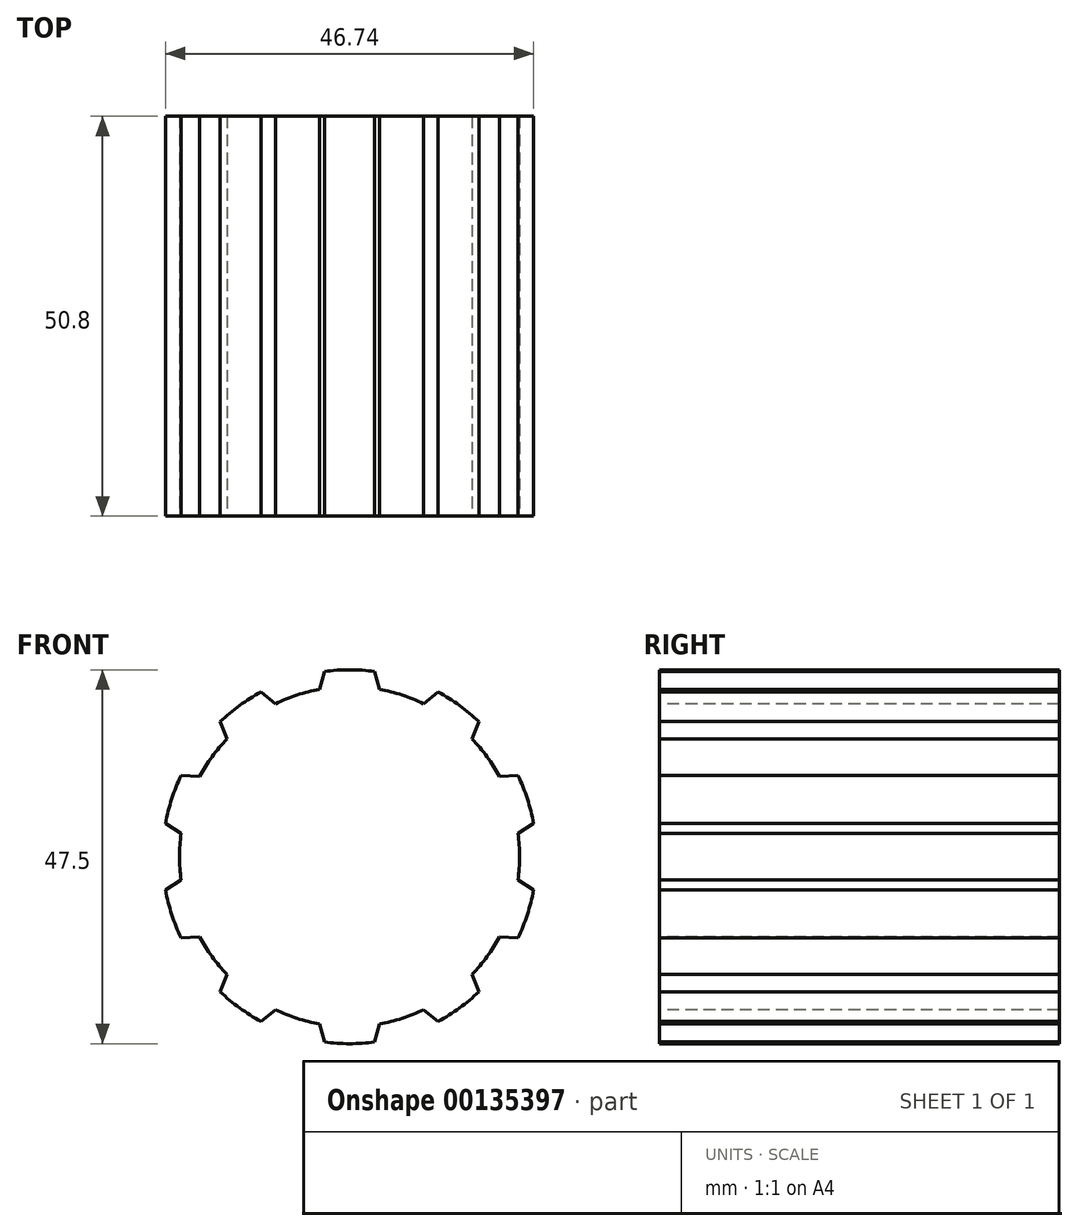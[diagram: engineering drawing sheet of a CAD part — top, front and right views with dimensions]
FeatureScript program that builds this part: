
annotation { "Feature Type Name" : "Feature", "Feature Type Description" : "" }
export const myFeature = defineFeature(function(context is Context, id is Id, definition is map)
    precondition{}
    {
        {
            var Q0;
            Q0=qCreatedBy(makeId("Front.planeOp"),FACE);
            var sketch = newSketch(context, id + "F0", { "sketchPlane" : qUnion([Q0])});
            skCircle(sketch, "E0", {"center": v(0, 0) * mm, "radius": 21.59 * mm});
            skArc(sketch, "E1", {"start": v(3.2, 23.53) * mm, "mid": v(0, 23.75) * mm, "end": v(-3.2, 23.53) * mm});
            skLineSegment(sketch, "E2", {"start": v(0, 0) * mm, "end": v(0, 31.16) * mm, "construction": true});
            skLineSegment(sketch, "E3", {"start": v(-3.81, 21.25) * mm, "end": v(-3.2, 23.53) * mm});
            skLineSegment(sketch, "E4.MirrorCS", {"start": v(3.81, 21.25) * mm, "end": v(3.2, 23.53) * mm});
            skLineSegment(sketch, "E5.1.0", {"start": v(-9.4, 19.43) * mm, "end": v(-11.24, 20.92) * mm});
            skArc(sketch, "E5.1.1", {"start": v(-11.24, 20.92) * mm, "mid": v(-13.96, 19.21) * mm, "end": v(-16.42, 17.16) * mm});
            skLineSegment(sketch, "E5.1.2", {"start": v(-15.57, 14.95) * mm, "end": v(-16.42, 17.16) * mm});
            skLineSegment(sketch, "E5.2.0", {"start": v(-19.03, 10.2) * mm, "end": v(-21.4, 10.31) * mm});
            skArc(sketch, "E5.2.1", {"start": v(-21.4, 10.31) * mm, "mid": v(-22.59, 7.34) * mm, "end": v(-23.37, 4.23) * mm});
            skLineSegment(sketch, "E5.2.2", {"start": v(-21.39, 2.94) * mm, "end": v(-23.37, 4.23) * mm});
            skLineSegment(sketch, "E6.1.3.0", {"start": v(-21.39, -2.94) * mm, "end": v(-23.37, -4.23) * mm});
            skArc(sketch, "E6.3.3.0", {"start": v(-23.37, -4.23) * mm, "mid": v(-22.59, -7.34) * mm, "end": v(-21.4, -10.31) * mm});
            skLineSegment(sketch, "E6.7.3.0", {"start": v(-19.03, -10.2) * mm, "end": v(-21.4, -10.31) * mm});
            skLineSegment(sketch, "E6.1.4.0", {"start": v(-15.57, -14.95) * mm, "end": v(-16.42, -17.16) * mm});
            skArc(sketch, "E6.3.4.0", {"start": v(-16.42, -17.16) * mm, "mid": v(-13.96, -19.21) * mm, "end": v(-11.24, -20.92) * mm});
            skLineSegment(sketch, "E6.7.4.0", {"start": v(-9.4, -19.43) * mm, "end": v(-11.24, -20.92) * mm});
            skLineSegment(sketch, "E6.1.5.0", {"start": v(-3.81, -21.25) * mm, "end": v(-3.2, -23.53) * mm});
            skArc(sketch, "E6.3.5.0", {"start": v(-3.2, -23.53) * mm, "mid": v(0, -23.75) * mm, "end": v(3.2, -23.53) * mm});
            skLineSegment(sketch, "E6.7.5.0", {"start": v(3.81, -21.25) * mm, "end": v(3.2, -23.53) * mm});
            skLineSegment(sketch, "E6.1.6.0", {"start": v(9.4, -19.43) * mm, "end": v(11.24, -20.92) * mm});
            skArc(sketch, "E6.3.6.0", {"start": v(11.24, -20.92) * mm, "mid": v(13.96, -19.21) * mm, "end": v(16.42, -17.16) * mm});
            skLineSegment(sketch, "E6.7.6.0", {"start": v(15.57, -14.95) * mm, "end": v(16.42, -17.16) * mm});
            skLineSegment(sketch, "E6.1.7.0", {"start": v(19.03, -10.2) * mm, "end": v(21.4, -10.31) * mm});
            skArc(sketch, "E6.3.7.0", {"start": v(21.4, -10.31) * mm, "mid": v(22.59, -7.34) * mm, "end": v(23.37, -4.23) * mm});
            skLineSegment(sketch, "E6.7.7.0", {"start": v(21.39, -2.94) * mm, "end": v(23.37, -4.23) * mm});
            skLineSegment(sketch, "E6.1.8.0", {"start": v(21.39, 2.94) * mm, "end": v(23.37, 4.23) * mm});
            skArc(sketch, "E6.3.8.0", {"start": v(23.37, 4.23) * mm, "mid": v(22.59, 7.34) * mm, "end": v(21.4, 10.31) * mm});
            skLineSegment(sketch, "E6.7.8.0", {"start": v(19.03, 10.2) * mm, "end": v(21.4, 10.31) * mm});
            skLineSegment(sketch, "E6.1.9.0", {"start": v(15.57, 14.95) * mm, "end": v(16.42, 17.16) * mm});
            skArc(sketch, "E6.3.9.0", {"start": v(16.42, 17.16) * mm, "mid": v(13.96, 19.21) * mm, "end": v(11.24, 20.92) * mm});
            skLineSegment(sketch, "E6.7.9.0", {"start": v(9.4, 19.43) * mm, "end": v(11.24, 20.92) * mm});
            skSolve(sketch);
        }
        {
            var Q0;
            {var subQ0=sQuery(id+"F0.wireOp",EDGE,"E0");var subQ3=makeQuery(id+"F0.imprint","INTERSECT",VERTEX,{"derivedFrom":[subQ0,sQuery(id+"F0.wireOp",EDGE,"E6.1.8.0")]});Q0=makeQuery(id+"F0.imprint","IMPRINT",FACE,{"disambiguationData":[TD([[makeQuery(id+"F0.imprint","IMPRINT",EDGE,{"disambiguationData":[TD([[subQ3,-1.0]])],"derivedFrom":subQ0}),1.0]])]});}
            var Q1;
            Q1=makeQuery(id+"F0.imprint","IMPRINT",FACE,{"disambiguationData":[TD([[makeQuery(id+"F0.imprint","IMPRINT",EDGE,{"derivedFrom":sQuery(id+"F0.wireOp",EDGE,"E1")}),1.0]])]});
            var Q2;
            {var subQ0=sQuery(id+"F0.wireOp",EDGE,"E6.1.9.0");Q2=makeQuery(id+"F0.imprint","IMPRINT",FACE,{"disambiguationData":[TD([[makeQuery(id+"F0.imprint","IMPRINT",EDGE,{"derivedFrom":subQ0}),1.0]])]});}
            var Q3;
            {var subQ0=sQuery(id+"F0.wireOp",EDGE,"E6.1.8.0");Q3=makeQuery(id+"F0.imprint","IMPRINT",FACE,{"disambiguationData":[TD([[makeQuery(id+"F0.imprint","IMPRINT",EDGE,{"derivedFrom":subQ0}),1.0]])]});}
            var Q4;
            {var subQ0=sQuery(id+"F0.wireOp",EDGE,"E6.1.7.0");Q4=makeQuery(id+"F0.imprint","IMPRINT",FACE,{"disambiguationData":[TD([[makeQuery(id+"F0.imprint","IMPRINT",EDGE,{"derivedFrom":subQ0}),1.0]])]});}
            var Q5;
            {var subQ0=sQuery(id+"F0.wireOp",EDGE,"E6.1.6.0");Q5=makeQuery(id+"F0.imprint","IMPRINT",FACE,{"disambiguationData":[TD([[makeQuery(id+"F0.imprint","IMPRINT",EDGE,{"derivedFrom":subQ0}),1.0]])]});}
            var Q6;
            {var subQ0=sQuery(id+"F0.wireOp",EDGE,"E6.1.5.0");Q6=makeQuery(id+"F0.imprint","IMPRINT",FACE,{"disambiguationData":[TD([[makeQuery(id+"F0.imprint","IMPRINT",EDGE,{"derivedFrom":subQ0}),1.0]])]});}
            var Q7;
            {var subQ0=sQuery(id+"F0.wireOp",EDGE,"E6.1.4.0");Q7=makeQuery(id+"F0.imprint","IMPRINT",FACE,{"disambiguationData":[TD([[makeQuery(id+"F0.imprint","IMPRINT",EDGE,{"derivedFrom":subQ0}),1.0]])]});}
            var Q8;
            {var subQ0=sQuery(id+"F0.wireOp",EDGE,"E6.1.3.0");Q8=makeQuery(id+"F0.imprint","IMPRINT",FACE,{"disambiguationData":[TD([[makeQuery(id+"F0.imprint","IMPRINT",EDGE,{"derivedFrom":subQ0}),1.0]])]});}
            var Q9;
            {var subQ0=sQuery(id+"F0.wireOp",EDGE,"E5.2.0");Q9=makeQuery(id+"F0.imprint","IMPRINT",FACE,{"disambiguationData":[TD([[makeQuery(id+"F0.imprint","IMPRINT",EDGE,{"derivedFrom":subQ0}),1.0]])]});}
            var Q10;
            {var subQ0=sQuery(id+"F0.wireOp",EDGE,"E5.1.0");Q10=makeQuery(id+"F0.imprint","IMPRINT",FACE,{"disambiguationData":[TD([[makeQuery(id+"F0.imprint","IMPRINT",EDGE,{"derivedFrom":subQ0}),1.0]])]});}
            extrude(context, id + "F1", {"entities" : qUnion([Q0, Q1, Q2, Q3, Q4, Q5, Q6, Q7, Q8, Q9, Q10]), "oppositeDirection" : true, "depth" : 50.8 * mm});
        }
    });
